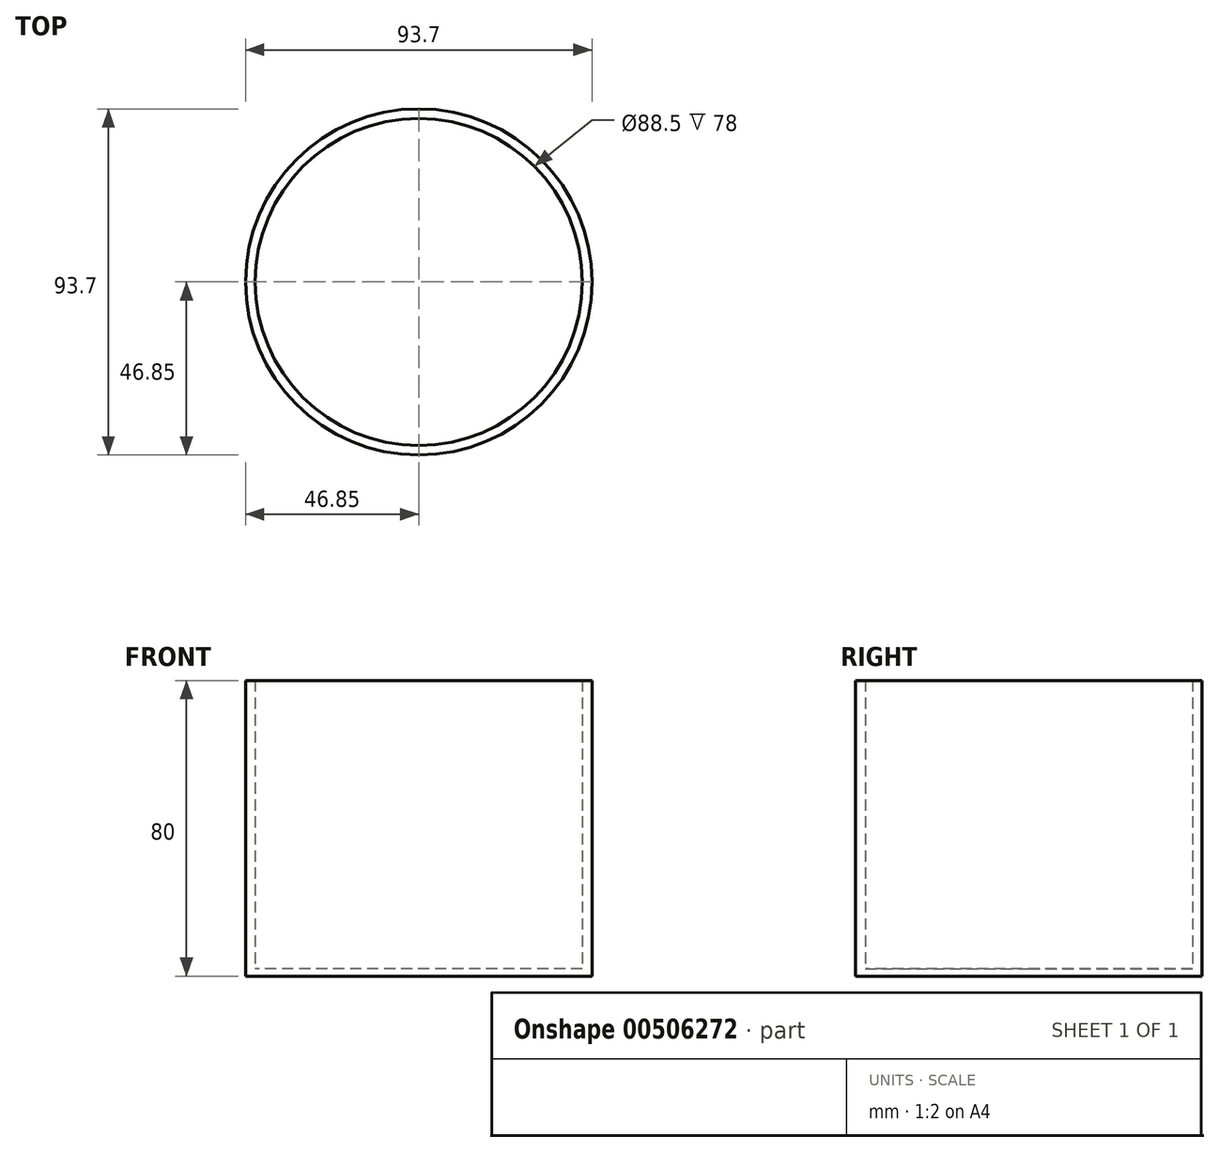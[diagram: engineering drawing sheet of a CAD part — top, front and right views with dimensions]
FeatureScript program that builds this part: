
annotation { "Feature Type Name" : "Feature", "Feature Type Description" : "" }
export const myFeature = defineFeature(function(context is Context, id is Id, definition is map)
    precondition{}
    {
        {
            var Q0;
            Q0=qCreatedBy(makeId("Top.planeOp"),FACE);
            var sketch = newSketch(context, id + "F0", { "sketchPlane" : qUnion([Q0])});
            skCircle(sketch, "E0", {"center": v(0, 0) * mm, "radius": 44.25 * mm});
            skCircle(sketch, "E1.0", {"center": v(0, 0) * mm, "radius": 46.85 * mm});
            skSolve(sketch);
        }
        {
            var Q0;
            Q0=makeQuery(id+"F0.imprint","IMPRINT",FACE,{"disambiguationData":[TD([[makeQuery(id+"F0.imprint","IMPRINT",EDGE,{"derivedFrom":sQuery(id+"F0.wireOp",EDGE,"E0")}),1.0]])]});
            extrude(context, id + "F1", {"entities" : qUnion([Q0]), "depth" : 2 * mm, "offsetDistance" : 25 * mm});
        }
        {
            var Q0;
            Q0 = qSketchRegion(id + "F0", true);
            extrude(context, id + "F2", {"entities" : qUnion([Q0]), "operationType" : NewBodyOperationType.ADD, "depth" : 80 * mm, "offsetDistance" : 25 * mm});
        }
    });
